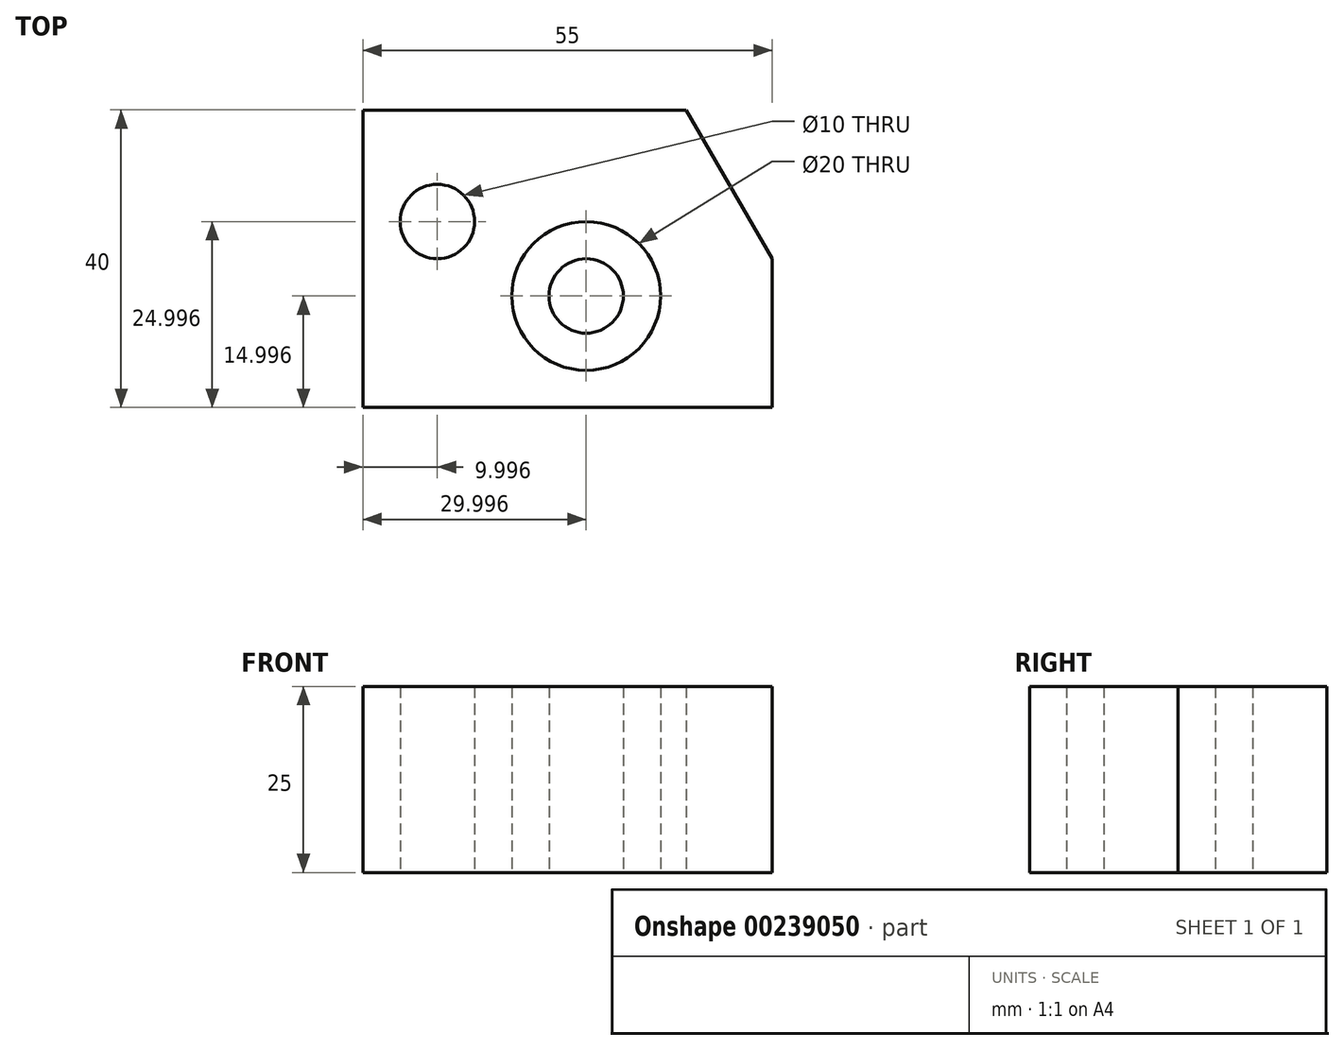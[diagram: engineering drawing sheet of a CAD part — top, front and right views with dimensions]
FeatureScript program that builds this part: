
annotation { "Feature Type Name" : "Feature", "Feature Type Description" : "" }
export const myFeature = defineFeature(function(context is Context, id is Id, definition is map)
    precondition{}
    {
        {
            var Q0;
            Q0=qCreatedBy(makeId("Top.planeOp"),FACE);
            var sketch = newSketch(context, id + "F0", { "sketchPlane" : qUnion([Q0])});
            skLineSegment(sketch, "E0", {"start": v(-76.22, -36.02) * mm, "end": v(-21.22, -36.02) * mm});
            skLineSegment(sketch, "E1", {"start": v(-21.22, -36.02) * mm, "end": v(-21.22, -16.02) * mm});
            skLineSegment(sketch, "E2", {"start": v(-32.77, 3.98) * mm, "end": v(-76.22, 3.98) * mm});
            skLineSegment(sketch, "E3", {"start": v(-76.22, 3.98) * mm, "end": v(-76.22, -36.02) * mm});
            skLineSegment(sketch, "E4", {"start": v(-76.22, -36.02) * mm, "end": v(-76.22, -11.02) * mm});
            skLineSegment(sketch, "E5", {"start": v(-76.22, -36.02) * mm, "end": v(-76.22, -11.02) * mm, "construction": true});
            skLineSegment(sketch, "E6", {"start": v(-76.22, -11.02) * mm, "end": v(-66.22, -11.02) * mm, "construction": true});
            skLineSegment(sketch, "E7", {"start": v(-76.22, -36.02) * mm, "end": v(-46.22, -36.02) * mm, "construction": true});
            skLineSegment(sketch, "E8", {"start": v(-46.22, -36.02) * mm, "end": v(-46.22, -21.02) * mm, "construction": true});
            skCircle(sketch, "E9", {"center": v(-66.22, -11.02) * mm, "radius": 5 * mm});
            skCircle(sketch, "E10", {"center": v(-46.22, -21.02) * mm, "radius": 5 * mm});
            skCircle(sketch, "E11", {"center": v(-46.22, -21.02) * mm, "radius": 10 * mm});
            skLineSegment(sketch, "E12", {"start": v(-21.22, -36.02) * mm, "end": v(-21.22, -16.02) * mm, "construction": true});
            skLineSegment(sketch, "E13", {"start": v(-21.22, -16.02) * mm, "end": v(-32.77, 3.98) * mm});
            skLineSegment(sketch, "E14", {"start": v(-21.22, -16.02) * mm, "end": v(-21.22, 3.98) * mm, "construction": true});
            skSolve(sketch);
        }
        {
            var Q0;
            Q0 = qSketchRegion(id + "F0", true);
            var Q1;
            Q1=makeQuery(id+"F0.imprint","IMPRINT",FACE,{"disambiguationData":[TD([[makeQuery(id+"F0.imprint","IMPRINT",EDGE,{"derivedFrom":sQuery(id+"F0.wireOp",EDGE,"E10")}),1.0]])]});
            extrude(context, id + "F1", {"entities" : qUnion([Q0, Q1]), "depth" : 25 * mm});
        }
    });
